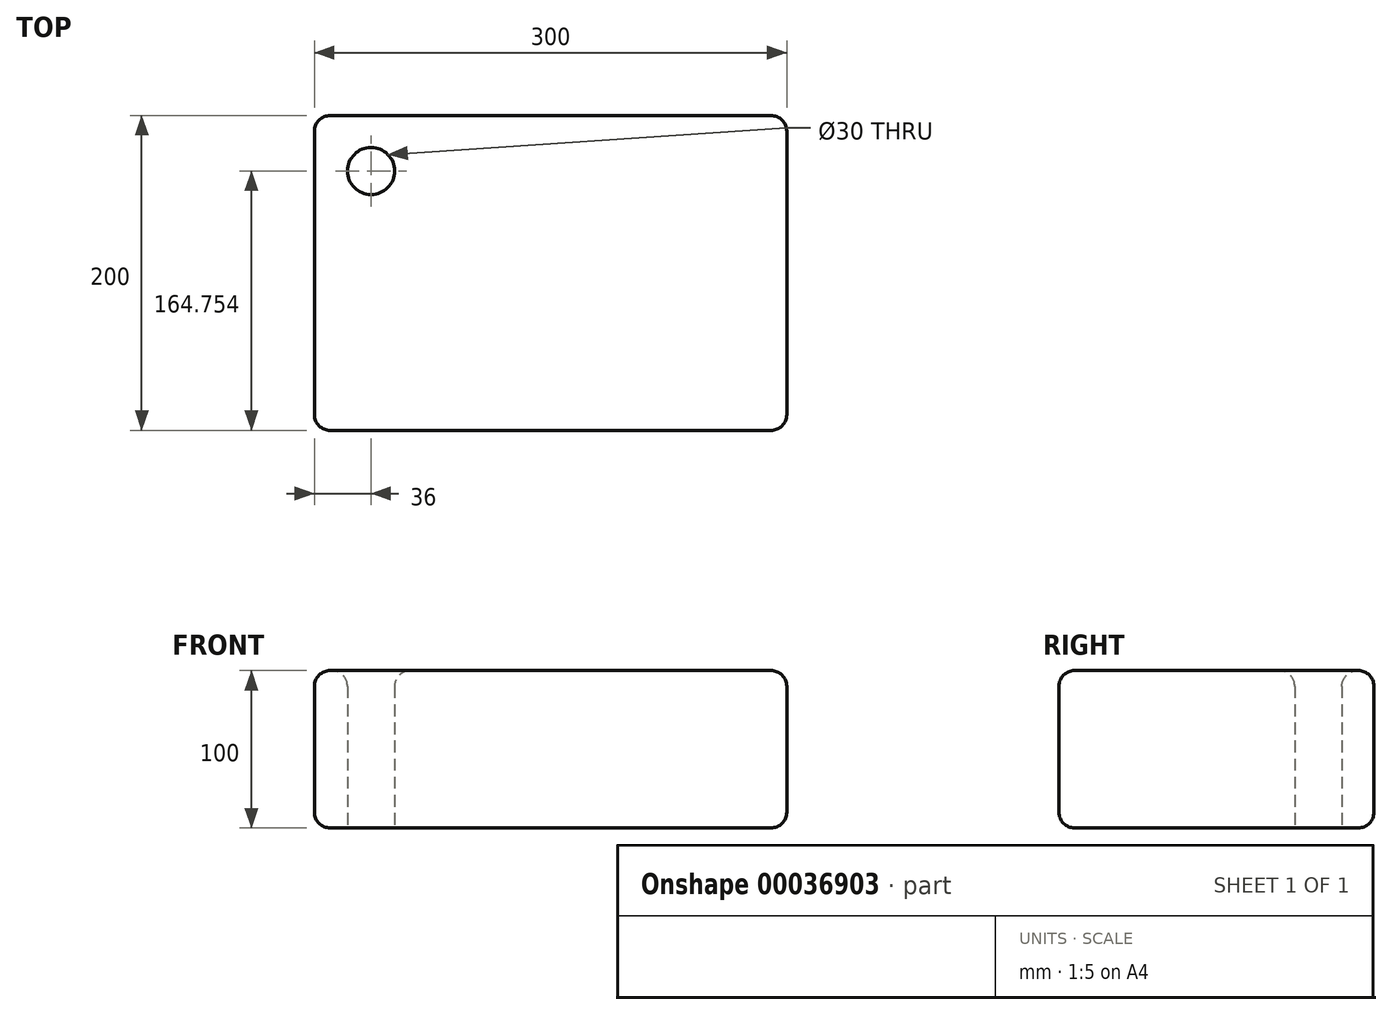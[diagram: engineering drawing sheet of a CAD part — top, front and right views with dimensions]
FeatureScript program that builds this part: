
annotation { "Feature Type Name" : "Feature", "Feature Type Description" : "" }
export const myFeature = defineFeature(function(context is Context, id is Id, definition is map)
    precondition{}
    {
        {
            var Q0;
            Q0=qCreatedBy(makeId("Top.planeOp"),FACE);
            var sketch = newSketch(context, id + "F0", { "sketchPlane" : qUnion([Q0])});
            skLineSegment(sketch, "E0.bottom", {"start": v(-164.6, 104.23) * mm, "end": v(135.4, 104.23) * mm});
            skLineSegment(sketch, "E0.top", {"start": v(-164.6, -95.77) * mm, "end": v(135.4, -95.77) * mm});
            skLineSegment(sketch, "E0.left", {"start": v(-164.6, 104.23) * mm, "end": v(-164.6, -95.77) * mm});
            skLineSegment(sketch, "E0.right", {"start": v(135.4, 104.23) * mm, "end": v(135.4, -95.77) * mm});
            skCircle(sketch, "E1", {"center": v(-128.6, 68.98) * mm, "radius": 15 * mm});
            skSolve(sketch);
        }
        {
            var Q0;
            Q0=makeQuery(id+"F0.imprint","IMPRINT",FACE,{"disambiguationData":[TD([[makeQuery(id+"F0.imprint","IMPRINT",EDGE,{"derivedFrom":sQuery(id+"F0.wireOp",EDGE,"E0.bottom")}),-1.0]])]});
            extrude(context, id + "F1", {"entities" : qUnion([Q0]), "depth" : 100 * mm});
        }
        {
            var Q0;
            Q0=makeQuery(id+"F1.opExtrude","SWEPT_EDGE",EDGE,{"disambiguationData":[OSD([sQuery(id+"F0.wireOp",EDGE,"E0.bottom"),sQuery(id+"F0.wireOp",EDGE,"E0.left")])]});
            var Q1;
            Q1=makeQuery(id+"F1.opExtrude","CAP_EDGE",EDGE,{"disambiguationData":[OSD([sQuery(id+"F0.wireOp",EDGE,"E0.bottom")])],"isStart":false});
            var Q2;
            Q2=makeQuery(id+"F1.opExtrude","SWEPT_EDGE",EDGE,{"disambiguationData":[OSD([sQuery(id+"F0.wireOp",EDGE,"E0.bottom"),sQuery(id+"F0.wireOp",EDGE,"E0.right")])]});
            var Q3;
            Q3=makeQuery(id+"F1.opExtrude","CAP_EDGE",EDGE,{"disambiguationData":[OSD([sQuery(id+"F0.wireOp",EDGE,"E0.right")])],"isStart":false});
            var Q4;
            Q4=makeQuery(id+"F1.opExtrude","CAP_EDGE",EDGE,{"disambiguationData":[OSD([sQuery(id+"F0.wireOp",EDGE,"E0.left")])],"isStart":false});
            var Q5;
            Q5=makeQuery(id+"F1.opExtrude","CAP_EDGE",EDGE,{"disambiguationData":[OSD([sQuery(id+"F0.wireOp",EDGE,"E1")])],"isStart":false});
            var Q6;
            Q6=makeQuery(id+"F1.opExtrude","SWEPT_EDGE",EDGE,{"disambiguationData":[OSD([sQuery(id+"F0.wireOp",EDGE,"E0.top"),sQuery(id+"F0.wireOp",EDGE,"E0.right")])]});
            var Q7;
            Q7=makeQuery(id+"F1.opExtrude","CAP_EDGE",EDGE,{"disambiguationData":[OSD([sQuery(id+"F0.wireOp",EDGE,"E0.top")])],"isStart":false});
            fillet(context, id + "F2", {"entities" : qUnion([Q0, Q1, Q2, Q3, Q4, Q5, Q6, Q7]), "radius" : 10 * mm, "tangentPropagation" : true, "allowEdgeOverflow" : false});
        }
        {
            var Q0;
            {var subQ0=sQuery(id+"F0.wireOp",EDGE,"E0.left");Q0=makeQuery(id+"F2.opFillet","BLEND_EDGE",EDGE,{"blendedFrom":[makeQuery(id+"F1.opExtrude","CAP_EDGE",EDGE,{"disambiguationData":[OSD([subQ0])],"isStart":false}),makeQuery(id+"F1.opExtrude","CAP_FACE",FACE,{"disambiguationData":[OSD([sQuery(id+"F0.wireOp",EDGE,"E0.bottom"),sQuery(id+"F0.wireOp",EDGE,"E0.top"),subQ0,sQuery(id+"F0.wireOp",EDGE,"E0.right"),sQuery(id+"F0.wireOp",EDGE,"E1")])],"isStart":false})],"blendedInto":[makeQuery(id+"F1.opExtrude","CAP_FACE",FACE,{"disambiguationData":[OSD([sQuery(id+"F0.wireOp",EDGE,"E0.bottom"),sQuery(id+"F0.wireOp",EDGE,"E0.top"),subQ0,sQuery(id+"F0.wireOp",EDGE,"E0.right"),sQuery(id+"F0.wireOp",EDGE,"E1")])],"isStart":false})]});}
            var Q1;
            Q1=makeQuery(id+"F2.opFillet","BLEND_EDGE",EDGE,{"blendedFrom":[makeQuery(id+"F1.opExtrude","CAP_EDGE",EDGE,{"disambiguationData":[OSD([sQuery(id+"F0.wireOp",EDGE,"E0.top")])],"isStart":false}),makeQuery(id+"F1.opExtrude","CAP_EDGE",EDGE,{"disambiguationData":[OSD([sQuery(id+"F0.wireOp",EDGE,"E0.left")])],"isStart":false})],"blendedInto":[]});
            var Q2;
            {var subQ0=sQuery(id+"F0.wireOp",EDGE,"E0.top");Q2=makeQuery(id+"F2.opFillet","BLEND_EDGE",EDGE,{"blendedFrom":[makeQuery(id+"F1.opExtrude","CAP_EDGE",EDGE,{"disambiguationData":[OSD([subQ0])],"isStart":false}),makeQuery(id+"F1.opExtrude","CAP_FACE",FACE,{"disambiguationData":[OSD([sQuery(id+"F0.wireOp",EDGE,"E0.bottom"),subQ0,sQuery(id+"F0.wireOp",EDGE,"E0.left"),sQuery(id+"F0.wireOp",EDGE,"E0.right"),sQuery(id+"F0.wireOp",EDGE,"E1")])],"isStart":false})],"blendedInto":[makeQuery(id+"F1.opExtrude","CAP_FACE",FACE,{"disambiguationData":[OSD([sQuery(id+"F0.wireOp",EDGE,"E0.bottom"),subQ0,sQuery(id+"F0.wireOp",EDGE,"E0.left"),sQuery(id+"F0.wireOp",EDGE,"E0.right"),sQuery(id+"F0.wireOp",EDGE,"E1")])],"isStart":false})]});}
            fillet(context, id + "F3", {"entities" : qUnion([Q0, Q1, Q2]), "radius" : 10 * mm, "tangentPropagation" : true, "allowEdgeOverflow" : false});
        }
        {
            var Q0;
            {var subQ0=sQuery(id+"F0.wireOp",EDGE,"E0.bottom");Q0=makeQuery(id+"F2.opFillet","BLEND_EDGE",EDGE,{"blendedFrom":[makeQuery(id+"F1.opExtrude","SWEPT_EDGE",EDGE,{"disambiguationData":[OSD([subQ0,sQuery(id+"F0.wireOp",EDGE,"E0.right")])]}),makeQuery(id+"F1.opExtrude","SWEPT_FACE",FACE,{"disambiguationData":[OSD([subQ0])]})],"blendedInto":[makeQuery(id+"F1.opExtrude","SWEPT_FACE",FACE,{"disambiguationData":[OSD([subQ0])]})]});}
            var Q1;
            {var subQ0=sQuery(id+"F0.wireOp",EDGE,"E0.right");Q1=makeQuery(id+"F2.opFillet","BLEND_EDGE",EDGE,{"blendedFrom":[makeQuery(id+"F1.opExtrude","SWEPT_EDGE",EDGE,{"disambiguationData":[OSD([sQuery(id+"F0.wireOp",EDGE,"E0.bottom"),subQ0])]}),makeQuery(id+"F1.opExtrude","SWEPT_FACE",FACE,{"disambiguationData":[OSD([subQ0])]})],"blendedInto":[makeQuery(id+"F1.opExtrude","SWEPT_FACE",FACE,{"disambiguationData":[OSD([subQ0])]})]});}
            var Q2;
            {var subQ0=sQuery(id+"F0.wireOp",EDGE,"E0.bottom");Q2=makeQuery(id+"F2.opFillet","BLEND_EDGE",EDGE,{"blendedFrom":[makeQuery(id+"F1.opExtrude","SWEPT_EDGE",EDGE,{"disambiguationData":[OSD([subQ0,sQuery(id+"F0.wireOp",EDGE,"E0.left")])]}),makeQuery(id+"F1.opExtrude","SWEPT_FACE",FACE,{"disambiguationData":[OSD([subQ0])]})],"blendedInto":[makeQuery(id+"F1.opExtrude","SWEPT_FACE",FACE,{"disambiguationData":[OSD([subQ0])]})]});}
            var Q3;
            {var subQ0=sQuery(id+"F0.wireOp",EDGE,"E0.bottom");var subQ1=sQuery(id+"F0.wireOp",EDGE,"E0.left");Q3=makeQuery(id+"F2.opFillet","BLEND_FACE",FACE,{"disambiguationData":[OSD([subQ0,subQ1]),TDD([makeQuery(id+"F1.opExtrude","SWEPT_EDGE",EDGE,{"disambiguationData":[OSD([subQ0,subQ1])]})])]});}
            var Q4;
            {var subQ0=sQuery(id+"F0.wireOp",EDGE,"E0.left");Q4=makeQuery(id+"F2.opFillet","BLEND_EDGE",EDGE,{"blendedFrom":[makeQuery(id+"F1.opExtrude","SWEPT_EDGE",EDGE,{"disambiguationData":[OSD([sQuery(id+"F0.wireOp",EDGE,"E0.bottom"),subQ0])]}),makeQuery(id+"F1.opExtrude","SWEPT_FACE",FACE,{"disambiguationData":[OSD([subQ0])]})],"blendedInto":[makeQuery(id+"F1.opExtrude","SWEPT_FACE",FACE,{"disambiguationData":[OSD([subQ0])]})]});}
            fillet(context, id + "F4", {"entities" : qUnion([Q0, Q1, Q2, Q3, Q4]), "radius" : 10 * mm, "tangentPropagation" : true, "allowEdgeOverflow" : false});
        }
    });
